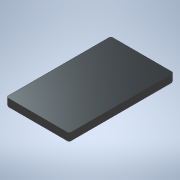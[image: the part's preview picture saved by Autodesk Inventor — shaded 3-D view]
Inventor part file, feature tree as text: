
AUTODESK INVENTOR PART (.ipt)
format: ipt  version: 2020 (Build 240168000, 168)  size: 137,728 bytes
history: native  units: mm
features: fillet x2, sketch x2, extrude x1, hole x1
ambient origin geometry x8: Origin, YZ Plane, XZ Plane, XY Plane, X Axis, Y Axis, Z Axis, Center Point
bodies: Solid1 (feature_tree)
feature tree (6):
  extrude  "Extrusion1"  Depth=487.3mm
  fillet  "Fillet1"  Radius=41.3mm
  fillet  "Fillet2"  Radius=10.0mm
  hole  "Hole1"  [1 undecoded]
  sketch  "Sketch1"  dims[d0=293.4mm d1=487.3mm d2=41.3mm d3=0.0mm d4=10.0mm]
  sketch  "Sketch2"  dims[d5=10.0mm d6=193.65mm d8=96.7mm d9=100.0mm d10=96.7mm d11=193.65mm d12=100.0mm d13=100.0mm d14=100.0mm d15=4.5mm d16=6.0mm d17=4.0mm d18=2.0mm d19=90.0deg d20=5.0mm d21=0.0mm]
note: 1 required parameter value undecoded (feature->parameter linkage not recoverable at this tier; creation-order binding heuristic only, values carry confidence <= 0.55)
